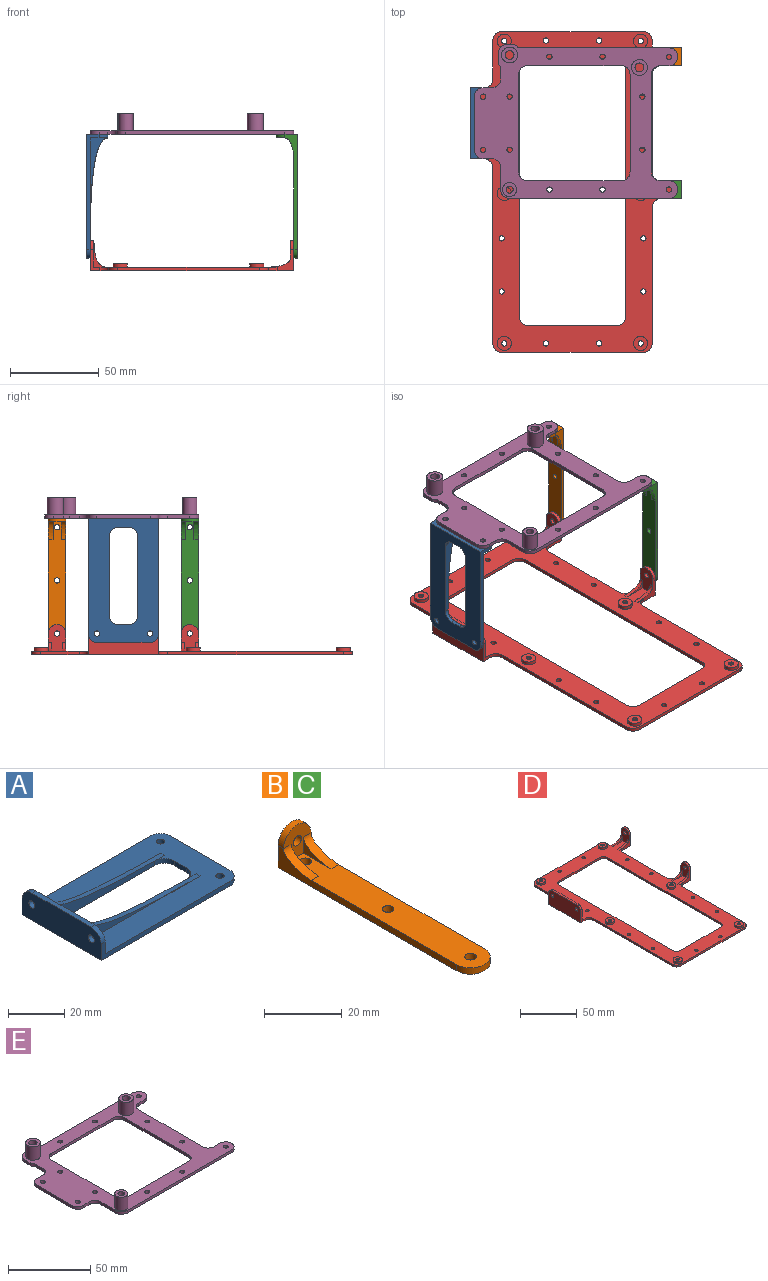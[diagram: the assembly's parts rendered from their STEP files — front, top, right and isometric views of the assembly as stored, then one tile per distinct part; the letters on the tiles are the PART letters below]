
ASSEMBLY  parts=5 mates=4
PART A: 31 faces, bbox 70.4x40.4x12.4 mm
  f0: plane 30x2mm, normal (1,0,0), area 60mm2, adj f4,f12,f27,f28
  f1: plane 16x10mm, normal (1,0,0), area 160mm2, adj f3,f9,f11,f14
  f2: plane 10x10mm, normal (1,0,0), area 87.6mm2, adj f4,f7,f14,f16,f20,f22
  f3: plane 16x8mm, normal (0,0,1), area 58.7mm2, adj f1,f8,f9,f11,f23,f26
  f4: plane 68.35x40.35mm, normal (0,0,1), area 1546mm2, adj f0,f2,f5,f7,f10,f13,f17,f18
  f5: plane 65x7mm, normal (0,1,0), area 140mm2, adj f4,f6,f12,f13,f21,f28
  f6: plane 40x12mm, normal (-1,0,0), area 455.1mm2, adj f5,f7,f12,f14,f15,f16,f21,f22
  f7: plane 65x7mm, normal (0,-1,0), area 140mm2, adj f2,f4,f6,f12,f22,f27
  f8: plane 6x2mm, normal (1,0,0), area 12mm2, adj f3,f12,f23,f26
  f9: plane 56.42x12mm, normal (0,-1,0), area 183.9mm2, adj f1,f3,f12,f23,f24,f29
  f10: plane 6x2mm, normal (-1,0,0), area 12mm2, adj f4,f12,f24,f25
  f11: plane 56.42x12mm, normal (0,1,0), area 183.9mm2, adj f1,f3,f12,f25,f26,f30
  f12: plane 70x40mm, normal (0,0,-1), area 1916.6mm2, adj f0,f5,f6,f7,f8,f9,f10,f11
  f13: plane 10x10mm, normal (1,0,0), area 87.6mm2, adj f4,f5,f14,f15,f19,f21
  f14: plane 30x2mm, normal (0,0,1), area 60mm2, adj f1,f2,f6,f13,f21,f22,f29,f30
  f15: cylinder r=1.5mm len=3mm, axis (1,0,0), area 18.8mm2, adj f6,f13
  f16: cylinder r=1.5mm len=3mm, axis (1,0,0), area 18.8mm2, adj f2,f6
  f17: cylinder r=1.5mm len=3mm, axis (0,0,-1), area 18.8mm2, adj f4,f12
  f18: cylinder r=1.5mm len=3mm, axis (0,0,-1), area 18.8mm2, adj f4,f12
  f19: plane 58x10mm, normal (0,1,0), area 93.9mm2, adj f4,f13,f29
  f20: plane 58x10mm, normal (0,-1,0), area 93.9mm2, adj f2,f4,f30
  f21: cylinder r=5mm len=5mm, axis (1,0,0), area 15.7mm2, adj f5,f6,f13,f14
  f22: cylinder r=5mm len=5mm, axis (-1,0,0), area 15.7mm2, adj f2,f6,f7,f14
  f23: cylinder r=5mm len=5mm, axis (0,0,-1), area 15.7mm2, adj f3,f8,f9,f12
  f24: cylinder r=5mm len=5mm, axis (0,0,1), area 15.7mm2, adj f4,f9,f10,f12
  f25: cylinder r=5mm len=5mm, axis (0,0,-1), area 15.7mm2, adj f4,f10,f11,f12
  f26: cylinder r=5mm len=5mm, axis (0,0,1), area 15.7mm2, adj f3,f8,f11,f12
  f27: cylinder r=5mm len=5mm, axis (0,0,1), area 15.7mm2, adj f0,f4,f7,f12
  f28: cylinder r=5mm len=5mm, axis (0,0,-1), area 15.7mm2, adj f0,f4,f5,f12
  f29: extruded ~58x10mm, area 122mm2, adj f4,f9,f14,f19
  f30: extruded ~58x10mm, area 122mm2, adj f4,f11,f14,f20
PART B: 16 faces, bbox 10x70x12 mm
  f0: plane 65x7mm, normal (-1,0,0), area 152.6mm2, adj f2,f4,f5,f10,f11,f15
  f1: plane 10x10mm, normal (0,-1,0), area 54.7mm2, adj f4,f6,f10,f12,f13,f14,f15
  f2: plane 12x10mm, normal (0,1,0), area 102.2mm2, adj f0,f3,f5,f6,f10
  f3: plane 65x7mm, normal (1,0,0), area 152.6mm2, adj f2,f4,f5,f10,f11,f14
  f4: plane 68x10mm, normal (0,0,1), area 593.1mm2, adj f0,f1,f3,f7,f8,f9,f11,f12
  f5: plane 70x10mm, normal (0,0,-1), area 668.1mm2, adj f0,f2,f3,f7,f8,f9,f11
  f6: cylinder r=1.5mm len=3mm, axis (0,-1,0), area 18.8mm2, adj f1,f2
  f7: cylinder r=1.5mm len=3mm, axis (0,0,-1), area 18.8mm2, adj f4,f5
  f8: cylinder r=1.5mm len=3mm, axis (0,0,-1), area 18.8mm2, adj f4,f5
  f9: cylinder r=1.5mm len=3mm, axis (0,0,-1), area 18.8mm2, adj f4,f5
  f10: cylinder r=5mm len=10mm, axis (0,1,0), area 31.4mm2, adj f0,f1,f2,f3
  f11: cylinder r=5mm len=10mm, axis (0,0,1), area 31.4mm2, adj f0,f3,f4,f5
  f12: plane 10x5mm, normal (1,0,0), area 12.6mm2, adj f1,f4,f15
  f13: plane 10x5mm, normal (-1,0,0), area 12.6mm2, adj f1,f4,f14
  f14: extruded ~10x5mm, area 32.7mm2, adj f1,f3,f4,f13
  f15: extruded ~10x5mm, area 32.7mm2, adj f0,f1,f4,f12
PART C: same geometry as B
PART D: 117 faces, bbox 115x181x17 mm
  f0: plane 14.47x12mm, normal (0,-1,0), area 52.2mm2, adj f2,f3,f18,f29,f76,f88,f113
  f1: plane 14.47x12mm, normal (0,1,0), area 62.2mm2, adj f4,f22,f23,f29,f77,f115
  f2: plane 181x111mm, normal (0,0,1), area 7275.9mm2, adj f0,f3,f4,f5,f6,f7,f8,f9
  f3: plane 15x10mm, normal (-1,0,0), area 112.2mm2, adj f0,f2,f19,f76,f107,f111,f112,f113
  f4: plane 15x10mm, normal (-1,0,0), area 112.2mm2, adj f1,f2,f21,f77,f108,f109,f110,f115
  f5: plane 15x8.53mm, normal (0,-1,0), area 20.4mm2, adj f2,f7,f102
  f6: plane 15x3mm, normal (1,0,0), area 45mm2, adj f2,f55,f99,f101
  f7: plane 15x10mm, normal (1,0,0), area 137.6mm2, adj f2,f5,f14,f55,f75,f79
  f8: plane 15x2mm, normal (1,0,0), area 30mm2, adj f2,f55,f95,f98
  f9: plane 15x2mm, normal (1,0,0), area 30mm2, adj f2,f55,f97,f100
  f10: plane 15x10mm, normal (1,0,0), area 137.6mm2, adj f2,f12,f55,f74,f78,f94
  f11: plane 21.8x2mm, normal (-1,0,0), area 43.6mm2, adj f2,f29,f84,f92
  f12: plane 12x5.53mm, normal (0,1,0), area 31.1mm2, adj f2,f10,f13,f29,f78,f84
  f13: plane 40x17mm, normal (-1,0,0), area 655.1mm2, adj f12,f14,f29,f55,f74,f75,f78,f79
  f14: plane 12x5.53mm, normal (0,-1,0), area 31.1mm2, adj f2,f7,f13,f29,f79,f85
  f15: plane 99.2x2mm, normal (-1,0,0), area 198.4mm2, adj f2,f29,f85,f86
  f16: plane 80x2mm, normal (0,-1,0), area 160mm2, adj f2,f29,f86,f87
  f17: plane 76.7x2mm, normal (1,0,0), area 153.4mm2, adj f2,f29,f87,f88
  f18: plane 17x10mm, normal (1,0,0), area 152.2mm2, adj f0,f19,f29,f76,f107
  f19: plane 14.47x12mm, normal (0,1,0), area 52.2mm2, adj f2,f3,f18,f29,f76,f89,f114
  f20: plane 55x2mm, normal (1,0,0), area 110mm2, adj f2,f29,f89,f90
  f21: plane 14.47x12mm, normal (0,-1,0), area 52.2mm2, adj f2,f4,f22,f29,f77,f90,f116
  f22: plane 17x10mm, normal (1,0,0), area 152.2mm2, adj f1,f21,f29,f77,f108
  f23: plane 4.3x2mm, normal (1,0,0), area 8.6mm2, adj f1,f2,f29,f91
  f24: plane 141x2mm, normal (1,0,0), area 282mm2, adj f2,f29,f80,f83
  f25: plane 50x2mm, normal (0,-1,0), area 100mm2, adj f2,f29,f80,f81
  f26: plane 141x2mm, normal (-1,0,0), area 282mm2, adj f2,f29,f81,f82
  f27: plane 50x2mm, normal (0,1,0), area 100mm2, adj f2,f29,f82,f83
  f28: plane 80x2mm, normal (0,1,0), area 160mm2, adj f2,f29,f91,f92
  f29: plane 181x115mm, normal (0,0,-1), area 7712.9mm2, adj f0,f1,f11,f12,f13,f14,f15,f16
  f30: cylinder r=4mm len=8mm, axis (0,0,-1), area 50.3mm2, adj f2,f31
  f31: plane 8x8mm, normal (0,0,1), area 43.2mm2, adj f30,f56
  f32: cylinder r=4mm len=8mm, axis (0,0,-1), area 50.3mm2, adj f2,f33
  f33: plane 8x8mm, normal (0,0,1), area 43.2mm2, adj f32,f60
  f34: cylinder r=4mm len=8mm, axis (0,0,-1), area 50.3mm2, adj f2,f35
  f35: plane 8x8mm, normal (0,0,1), area 43.2mm2, adj f34,f59
  f36: cylinder r=4mm len=8mm, axis (0,0,-1), area 50.3mm2, adj f2,f37
  f37: plane 8x8mm, normal (0,0,1), area 43.2mm2, adj f36,f61
  f38: cylinder r=4mm len=8mm, axis (0,0,-1), area 50.3mm2, adj f2,f39
  f39: plane 8x8mm, normal (0,0,1), area 43.2mm2, adj f38,f58
  f40: cylinder r=4mm len=8mm, axis (0,0,-1), area 50.3mm2, adj f2,f41
  f41: plane 8x8mm, normal (0,0,1), area 43.2mm2, adj f40,f57
  f42: cylinder r=3mm len=6mm, axis (0,0,-1), area 56.5mm2, adj f29,f43
  f43: plane 6x6mm, normal (0,0,-1), area 21.2mm2, adj f42,f61
  f44: cylinder r=3mm len=6mm, axis (0,0,-1), area 56.5mm2, adj f29,f45
  f45: plane 6x6mm, normal (0,0,-1), area 21.2mm2, adj f44,f60
  f46: cylinder r=3mm len=6mm, axis (0,0,-1), area 56.5mm2, adj f29,f47
  f47: plane 6x6mm, normal (0,0,-1), area 21.2mm2, adj f46,f59
  f48: cylinder r=3mm len=6mm, axis (0,0,-1), area 56.5mm2, adj f29,f49
  f49: plane 6x6mm, normal (0,0,-1), area 21.2mm2, adj f48,f58
  f50: cylinder r=3mm len=6mm, axis (0,0,-1), area 56.5mm2, adj f29,f51
  f51: plane 6x6mm, normal (0,0,-1), area 21.2mm2, adj f50,f57
  f52: cylinder r=3mm len=6mm, axis (0,0,-1), area 56.5mm2, adj f29,f53
  f53: plane 6x6mm, normal (0,0,-1), area 21.2mm2, adj f52,f56
  f54: plane 15x3mm, normal (1,0,0), area 45mm2, adj f2,f55,f93,f96
  f55: plane 30x2mm, normal (0,0,1), area 60mm2, adj f6,f7,f8,f9,f10,f13,f54,f78
  f56: cylinder r=1.5mm len=3mm, axis (0,0,-1), area 9.4mm2, adj f31,f53
  f57: cylinder r=1.5mm len=3mm, axis (0,0,-1), area 9.4mm2, adj f41,f51
  f58: cylinder r=1.5mm len=3mm, axis (0,0,-1), area 9.4mm2, adj f39,f49
  f59: cylinder r=1.5mm len=3mm, axis (0,0,-1), area 9.4mm2, adj f35,f47
  f60: cylinder r=1.5mm len=3mm, axis (0,0,-1), area 9.4mm2, adj f33,f45
  f61: cylinder r=1.5mm len=3mm, axis (0,0,-1), area 9.4mm2, adj f37,f43
  f62: cylinder r=1.5mm len=3mm, axis (0,0,-1), area 18.8mm2, adj f2,f29
  f63: cylinder r=1.5mm len=3mm, axis (0,0,-1), area 18.8mm2, adj f2,f29
  f64: cylinder r=1.5mm len=3mm, axis (0,0,-1), area 18.8mm2, adj f2,f29
  f65: cylinder r=1.5mm len=3mm, axis (0,0,-1), area 18.8mm2, adj f2,f29
  f66: cylinder r=1.5mm len=3mm, axis (0,0,-1), area 18.8mm2, adj f2,f29
  f67: cylinder r=1.5mm len=3mm, axis (0,0,-1), area 18.8mm2, adj f2,f29
  f68: cylinder r=1.5mm len=3mm, axis (0,0,-1), area 18.8mm2, adj f2,f29
  f69: cylinder r=1.5mm len=3mm, axis (0,0,-1), area 18.8mm2, adj f2,f29
  f70: cylinder r=1.5mm len=3mm, axis (0,0,-1), area 18.8mm2, adj f2,f29
  f71: cylinder r=1.5mm len=3mm, axis (0,0,-1), area 18.8mm2, adj f2,f29
  f72: cylinder r=1.5mm len=3mm, axis (0,0,-1), area 18.8mm2, adj f2,f29
  f73: cylinder r=1.5mm len=3mm, axis (0,0,-1), area 18.8mm2, adj f2,f29
  f74: cylinder r=1.5mm len=3mm, axis (1,0,0), area 18.8mm2, adj f10,f13
  f75: cylinder r=1.5mm len=3mm, axis (1,0,0), area 18.8mm2, adj f7,f13
  f76: cylinder r=5mm len=10mm, axis (1,0,0), area 31.4mm2, adj f0,f3,f18,f19
  f77: cylinder r=5mm len=10mm, axis (1,0,0), area 31.4mm2, adj f1,f4,f21,f22
  f78: cylinder r=5mm len=5mm, axis (1,0,0), area 15.7mm2, adj f10,f12,f13,f55
  f79: cylinder r=5mm len=5mm, axis (-1,0,0), area 15.7mm2, adj f7,f13,f14,f55
  f80: cylinder r=5mm len=5mm, axis (0,0,-1), area 15.7mm2, adj f2,f24,f25,f29
  f81: cylinder r=5mm len=5mm, axis (0,0,1), area 15.7mm2, adj f2,f25,f26,f29
  f82: cylinder r=5mm len=5mm, axis (0,0,-1), area 15.7mm2, adj f2,f26,f27,f29
  f83: cylinder r=5mm len=5mm, axis (0,0,1), area 15.7mm2, adj f2,f24,f27,f29
  f84: cylinder r=5mm len=5mm, axis (0,0,1), area 15.7mm2, adj f2,f11,f12,f29
  f85: cylinder r=5mm len=5mm, axis (0,0,-1), area 15.7mm2, adj f2,f14,f15,f29
  f86: cylinder r=5mm len=5mm, axis (0,0,-1), area 15.7mm2, adj f2,f15,f16,f29
  f87: cylinder r=5mm len=5mm, axis (0,0,1), area 15.7mm2, adj f2,f16,f17,f29
  f88: cylinder r=5mm len=5mm, axis (0,0,-1), area 15.7mm2, adj f0,f2,f17,f29
  f89: cylinder r=5mm len=5mm, axis (0,0,-1), area 15.7mm2, adj f2,f19,f20,f29
  f90: cylinder r=5mm len=5mm, axis (0,0,1), area 15.7mm2, adj f2,f20,f21,f29
  f91: cylinder r=5mm len=5mm, axis (0,0,-1), area 15.7mm2, adj f2,f23,f28,f29
  f92: cylinder r=5mm len=5mm, axis (0,0,1), area 15.7mm2, adj f2,f11,f28,f29
  f93: plane 15x8.53mm, normal (0,-1,0), area 20.4mm2, adj f2,f54,f106
  f94: plane 15x8.53mm, normal (0,1,0), area 20.4mm2, adj f2,f10,f106
  f95: plane 15x8.53mm, normal (0,-1,0), area 20.4mm2, adj f2,f8,f105
  f96: plane 15x8.53mm, normal (0,1,0), area 20.4mm2, adj f2,f54,f105
  f97: plane 15x8.53mm, normal (0,-1,0), area 20.4mm2, adj f2,f9,f104
  f98: plane 15x8.53mm, normal (0,1,0), area 20.4mm2, adj f2,f8,f104
  f99: plane 15x8.53mm, normal (0,-1,0), area 20.4mm2, adj f2,f6,f103
  f100: plane 15x8.53mm, normal (0,1,0), area 20.4mm2, adj f2,f9,f103
  f101: plane 15x8.53mm, normal (0,1,0), area 20.4mm2, adj f2,f6,f102
  f102: extruded ~15x8.53mm, area 39.3mm2, adj f2,f5,f55,f101
  f103: extruded ~15x8.53mm, area 39.3mm2, adj f2,f55,f99,f100
  f104: extruded ~15x8.53mm, area 39.3mm2, adj f2,f55,f97,f98
  f105: extruded ~15x8.53mm, area 39.3mm2, adj f2,f55,f95,f96
  f106: extruded ~15x8.53mm, area 39.3mm2, adj f2,f55,f93,f94
  f107: cylinder r=1.5mm len=3mm, axis (-1,0,0), area 18.8mm2, adj f3,f18
  f108: cylinder r=1.5mm len=3mm, axis (-1,0,0), area 18.8mm2, adj f4,f22
  f109: plane 12.47x5mm, normal (0,1,0), area 13.3mm2, adj f2,f4,f116
  f110: plane 12.47x5mm, normal (0,-1,0), area 13.3mm2, adj f2,f4,f115
  f111: plane 12.47x5mm, normal (0,-1,0), area 13.3mm2, adj f2,f3,f114
  f112: plane 12.47x5mm, normal (0,1,0), area 13.3mm2, adj f2,f3,f113
  f113: extruded ~12.47x5mm, area 28.8mm2, adj f0,f2,f3,f112
  f114: extruded ~12.47x5mm, area 28.8mm2, adj f2,f3,f19,f111
  f115: extruded ~12.47x5mm, area 28.8mm2, adj f1,f2,f4,f110
  f116: extruded ~12.47x5mm, area 28.8mm2, adj f2,f4,f21,f109
PART E: 55 faces, bbox 115x87x12 mm
  f0: plane 55x2mm, normal (1,0,0), area 110mm2, adj f16,f17,f44,f47
  f1: plane 53x2mm, normal (0,-1,0), area 106mm2, adj f16,f17,f44,f45
  f2: plane 55x2mm, normal (-1,0,0), area 110mm2, adj f16,f17,f45,f46
  f3: plane 5x2mm, normal (0,1,0), area 10mm2, adj f16,f17,f39,f40
  f4: plane 55x2mm, normal (1,0,0), area 110mm2, adj f16,f17,f39,f49
  f5: plane 5x2mm, normal (0,-1,0), area 10mm2, adj f16,f17,f49,f50
  f6: plane 85x2mm, normal (0,1,0), area 170mm2, adj f16,f17,f41,f50
  f7: plane 2.32x2mm, normal (0,1,0), area 4.6mm2, adj f16,f17,f41,f42
  f8: plane 5.82x2mm, normal (-1,0,0), area 11.6mm2, adj f16,f17,f42,f43
  f9: plane 5.3x2mm, normal (-1,0,0), area 10.6mm2, adj f16,f17,f43,f51
  f10: plane 5x2mm, normal (0,1,0), area 10mm2, adj f16,f17,f51,f52
  f11: plane 30x2mm, normal (-1,0,0), area 60mm2, adj f16,f17,f52,f53
  f12: plane 5x2mm, normal (0,-1,0), area 10mm2, adj f16,f17,f53,f54
  f13: plane 12.5x2mm, normal (-1,0,0), area 25mm2, adj f16,f17,f48,f54
  f14: plane 90x2mm, normal (0,-1,0), area 180mm2, adj f16,f17,f40,f48
  f15: plane 53x2mm, normal (0,1,0), area 106mm2, adj f16,f17,f46,f47
  f16: plane 115x87.03mm, normal (0,0,1), area 3801.5mm2, adj f0,f1,f2,f3,f4,f5,f6,f7
  f17: plane 115x87.03mm, normal (0,0,-1), area 3927.2mm2, adj f0,f1,f2,f3,f4,f5,f6,f7
  f18: cylinder r=2.5mm len=12mm, axis (0,0,-1), area 188.5mm2, adj f17,f20
  f19: cylinder r=4.5mm len=10mm, axis (0,0,-1), area 282.7mm2, adj f16,f20
  f20: plane 9x9mm, normal (0,0,1), area 44mm2, adj f18,f19
  f21: cylinder r=2.5mm len=12mm, axis (0,0,-1), area 188.5mm2, adj f17,f23
  f22: cylinder r=4.5mm len=10mm, axis (0,0,-1), area 282.7mm2, adj f16,f23
  f23: plane 9x9mm, normal (0,0,1), area 44mm2, adj f21,f22
  f24: cylinder r=2mm len=12mm, axis (0,0,-1), area 150.8mm2, adj f17,f26
  f25: cylinder r=4mm len=10mm, axis (0,0,-1), area 251.3mm2, adj f16,f26
  f26: plane 8x8mm, normal (0,0,1), area 37.7mm2, adj f24,f25
  f27: cylinder r=1.5mm len=3mm, axis (0,0,-1), area 18.8mm2, adj f16,f17
  f28: cylinder r=1.5mm len=3mm, axis (0,0,-1), area 18.8mm2, adj f16,f17
  f29: cylinder r=1.5mm len=3mm, axis (0,0,-1), area 18.8mm2, adj f16,f17
  f30: cylinder r=1.5mm len=3mm, axis (0,0,-1), area 18.8mm2, adj f16,f17
  f31: cylinder r=1.5mm len=3mm, axis (0,0,-1), area 18.8mm2, adj f16,f17
  f32: cylinder r=1.5mm len=3mm, axis (0,0,-1), area 18.8mm2, adj f16,f17
  f33: cylinder r=1.5mm len=3mm, axis (0,0,-1), area 18.8mm2, adj f16,f17
  f34: cylinder r=1.5mm len=3mm, axis (0,0,-1), area 18.8mm2, adj f16,f17
  f35: cylinder r=1.5mm len=3mm, axis (0,0,-1), area 18.8mm2, adj f16,f17
  f36: cylinder r=1.5mm len=3mm, axis (0,0,-1), area 18.8mm2, adj f16,f17
  f37: cylinder r=1.5mm len=3mm, axis (0,0,-1), area 18.8mm2, adj f16,f17
  f38: cylinder r=1.5mm len=3mm, axis (0,0,-1), area 18.8mm2, adj f16,f17
  f39: cylinder r=5mm len=5mm, axis (0,0,-1), area 15.7mm2, adj f3,f4,f16,f17
  f40: cylinder r=5mm len=10mm, axis (0,0,-1), area 31.4mm2, adj f3,f14,f16,f17
  f41: cylinder r=5mm len=4.02mm, axis (0,0,-1), area 9.4mm2, adj f6,f7,f16,f17
  f42: cylinder r=5mm len=5mm, axis (0,0,-1), area 15.7mm2, adj f7,f8,f16,f17
  f43: cylinder r=5mm len=3.41mm, axis (0,0,-1), area 7.5mm2, adj f8,f9,f16,f17
  f44: cylinder r=5mm len=5mm, axis (0,0,-1), area 15.7mm2, adj f0,f1,f16,f17
  f45: cylinder r=5mm len=5mm, axis (0,0,1), area 15.7mm2, adj f1,f2,f16,f17
  f46: cylinder r=5mm len=5mm, axis (0,0,-1), area 15.7mm2, adj f2,f15,f16,f17
  f47: cylinder r=5mm len=5mm, axis (0,0,1), area 15.7mm2, adj f0,f15,f16,f17
  f48: cylinder r=5mm len=5mm, axis (0,0,-1), area 15.7mm2, adj f13,f14,f16,f17
  f49: cylinder r=5mm len=5mm, axis (0,0,1), area 15.7mm2, adj f4,f5,f16,f17
  f50: cylinder r=5mm len=10mm, axis (0,0,-1), area 31.4mm2, adj f5,f6,f16,f17
  f51: cylinder r=5mm len=5mm, axis (0,0,1), area 15.7mm2, adj f9,f10,f16,f17
  f52: cylinder r=5mm len=5mm, axis (0,0,-1), area 15.7mm2, adj f10,f11,f16,f17
  f53: cylinder r=5mm len=5mm, axis (0,0,-1), area 15.7mm2, adj f11,f12,f16,f17
  f54: cylinder r=5mm len=5mm, axis (0,0,1), area 15.7mm2, adj f12,f13,f16,f17
PLACE A rot(axis=(0,1,0),90deg) t=(-13.77,-27.61,100.22)mm
PLACE B rot(axis=(0.58,-0.58,-0.58),120deg) t=(105.23,9.89,79.84)mm
PLACE C rot(axis=(0.58,-0.58,-0.58),120deg) t=(105.23,-65.11,79.84)mm
PLACE D t=(43.76,-66.81,37.84)mm
PLACE E t=(45.73,-27.61,114.84)mm
MATE pin_slot C.f9 <-> D.f76  axis (-1,0,0) through (103.23,-65.11,49.84)mm
MATE pin_slot E.f30 <-> A.f16  axis (0,0,-1) through (-6.77,-42.61,114.84)mm
MATE pin_slot B.f11 <-> D.f77  axis (-1,0,0) through (103.23,9.89,49.84)mm
MATE pin_slot A.f17 <-> D.f75  axis (1,0,0) through (-11.77,-42.61,49.84)mm
